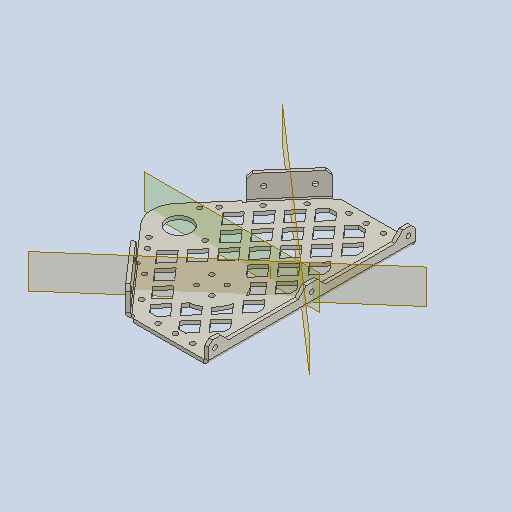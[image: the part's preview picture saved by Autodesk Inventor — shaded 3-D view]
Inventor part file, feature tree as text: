
AUTODESK INVENTOR PART (.ipt)
format: ipt  version: 2022 (Build 260153000, 153)  size: 846,848 bytes
history: native  units: in
note: dims shown in document units (in); Inventor stores cm internally (conversion verified against a paired STEP export)
features: other x17, sketch x15, sheet_metal_op x14, hole x7, plane x5, projected_geometry x4, reference x4, extrude x2, fillet x1, mirror x1
ambient origin geometry x8: Origin, YZ Plane, XZ Plane, XY Plane, X Axis, Y Axis, Z Axis, Center Point
bodies: Solid1 (feature_tree)
feature tree (70):
  sheet_metal_op  "Face1"
  other  "Work Axis1"
  sheet_metal_op  "Face2"
  sheet_metal_op  "Flange1"
  sheet_metal_op  "Flange2"
  sheet_metal_op  "Flange3"
  other  "Corner Chamfer1"
  hole  "Hole1"  [1 undecoded]
  extrude  "Extrusion1"  Depth=0.7874in
  extrude  "Extrusion2"  Depth=0.0312in
  hole  "Hole2"  [1 undecoded]
  hole  "Hole3"  [1 undecoded]
  hole  "Hole4"  [1 undecoded]
  plane  "Work Plane3"
  plane  "Work Plane4"
  plane  "Work Plane5"
  hole  "Hole5"  [1 undecoded]
  hole  "Hole6"  [1 undecoded]
  hole  "Hole7"  [1 undecoded]
  sheet_metal_op  "Face4"
  fillet  "Fillet1"  Radius=0.1024in
  mirror  "Mirror1"
  sketch  "Sketch1"  dims[d0=2.1654in d1=6.0in]
  other  "Plate1"
  plane  "Work Plane1"
  plane  "Work Plane2"
  sketch  "Sketch2"  dims[d2=0.1024in d3=0.7874in]
  other  "Plate2"
  sheet_metal_op  "Bend1"
  sketch  "Sketch3"  dims[d4=1.5748in d6=0.0312in]
  other  "Plate3"
  sheet_metal_op  "Bend2"
  sheet_metal_op  "Corner1"
  sketch  "Sketch4"  dims[d7=0.1024in d8=0.0512in]
  other  "Plate4"
  sheet_metal_op  "Bend3"
  sheet_metal_op  "Corner2"
  sketch  "Sketch5"  dims[d9=0.2047in d10=0.0312in]
  other  "Plate5"
  sheet_metal_op  "Bend4"
  sheet_metal_op  "Corner3"
  sketch  "Sketch6"  dims[d11=0.1024in d12=0.0512in]
  sketch  "Sketch7"  dims[d13=0.2047in d14=0.0312in]
  projected_geometry  "Projected Loop1"
  sketch  "Sketch8"  dims[d15=0.5906in d16=90.0deg d17=0.0312in d18=0.3071in]
  reference  "Reference1"
  sketch  "Sketch9"  dims[d19=0.0512in d20=0.0312in d21=0.1024in]
  reference  "Reference2"
  reference  "Reference3"
  reference  "Reference4"
  sketch  "Sketch12"  dims[d22=0.0512in]
  sketch  "Sketch13"  dims[d23=0.2047in]
  sketch  "Sketch14"  dims[d24=0.0312in]
  projected_geometry  "Projected Loop2"
  sketch  "Sketch15"  dims[d25=1.75in d26=0.1in]
  sketch  "Sketch16"  dims[d27=0.7819in d28=90.0deg d29=0.0312in]
  projected_geometry  "Projected Loop3"
  other  "Plate7"
  sheet_metal_op  "Bend6"
  sketch  "Sketch18"  dims[d30=0.3071in d31=0.0512in d32=0.0312in d33=0.1024in d34=0.0512in d35=0.2047in d36=0.0312in d37=1.75in d38=0.1in d39=0.7819in d40=90.0deg d41=0.0312in d42=0.3071in d43=0.0512in d44=0.0312in d45=0.125in d46=0.25in d47=45.0deg d48=0.7087in d49=0.75in d50=0.248in d51=0.25in d52=90.0deg d53=0.1024in d54=0.8108in d55=0.3937in d56=0.1969in d57=0.3937in d58=0.3937in d59=0.3937in d60=0.1969in d64=0.1969in d67=0.1969in d68=0.1969in d69=0.1969in d70=0.1969in d71=0.1969in d72=0.1969in d73=0.1969in d74=0.1969in d75=0.4329in d76=0.4329in d77=0.4329in d78=0.4329in d79=0.4329in d80=0.4329in d81=0.4048in d82=0.1969in d83=0.4329in d84=0.4329in d85=0.1969in d86=0.1969in d87=0.1969in d88=0.1969in d89=0.1969in d90=0.1969in d91=0.1969in d92=0.1969in d93=0.1969in d94=0.4329in d95=0.4329in d96=0.4329in d97=0.4329in d98=0.4329in d99=0.4329in d100=0.4329in d101=0.1969in d102=1.0in d103=0.0in d104=1.5748in d105=0.748in d106=0.6299in d107=45.0deg d113=1.0in d114=0.0in d115=0.142in d116=0.75in d117=0.248in d118=0.25in d119=90.0deg d120=1.0in d121=0.8108in d122=0.1417in d123=0.75in d124=0.375in d125=0.25in d126=0.5635in d127=0.1024in d128=0.0in d129=0.142in d130=0.75in d131=0.248in d132=0.25in d133=90.0deg d134=0.1024in d135=0.0in d136=0.1339in d137=0.75in d138=0.248in d139=0.25in d140=90.0deg d141=0.1024in d142=0.8108in d143=0.1339in d144=0.75in d145=0.375in d146=0.25in d147=0.5635in d148=0.1024in d149=0.8108in d150=0.2362in d151=0.2362in d152=0.2362in d153=0.2362in d154=0.408in d155=0.408in d156=0.408in d157=0.408in d158=0.408in d159=0.408in d160=0.408in d161=0.408in d162=0.408in d163=0.408in d168=0.1024in d169=0.0in d170=0.408in d171=0.408in d172=0.1969in d173=0.1969in d174=0.134in d175=0.75in d176=0.248in d177=0.25in d178=90.0deg d179=0.1024in d180=0.8108in d181=0.3937in d182=0.1969in d183=0.0312in d184=0.1024in d185=0.0512in d186=0.2047in d187=0.0312in d188=0.0625in d199=0.3937in d200=135.0deg d201=0.3937in d202=0.3937in d203=0.3937in d204=0.1024in d205=0.0in]
  projected_geometry  "Projected Loop5"
  other  "Cut1"
  other  "Cut3"
  parser-record x1  (decoder bookkeeping rows leaked as tree rows — omitted from the tree; the rows remain in map.json)
  other  "Main Body.iam"
  other  "Brushless Motor:1"
  other  "Top Stubstructure:1"
  other  "Mount Side:2"
  other  "Mount Side:1"
  other  "Definition1"
note: 7 required parameter values undecoded (feature->parameter linkage not recoverable at this tier; creation-order binding heuristic only, values carry confidence <= 0.55)
note: 1 file-system path scrubbed to <path> (originals preserved in map.json)
